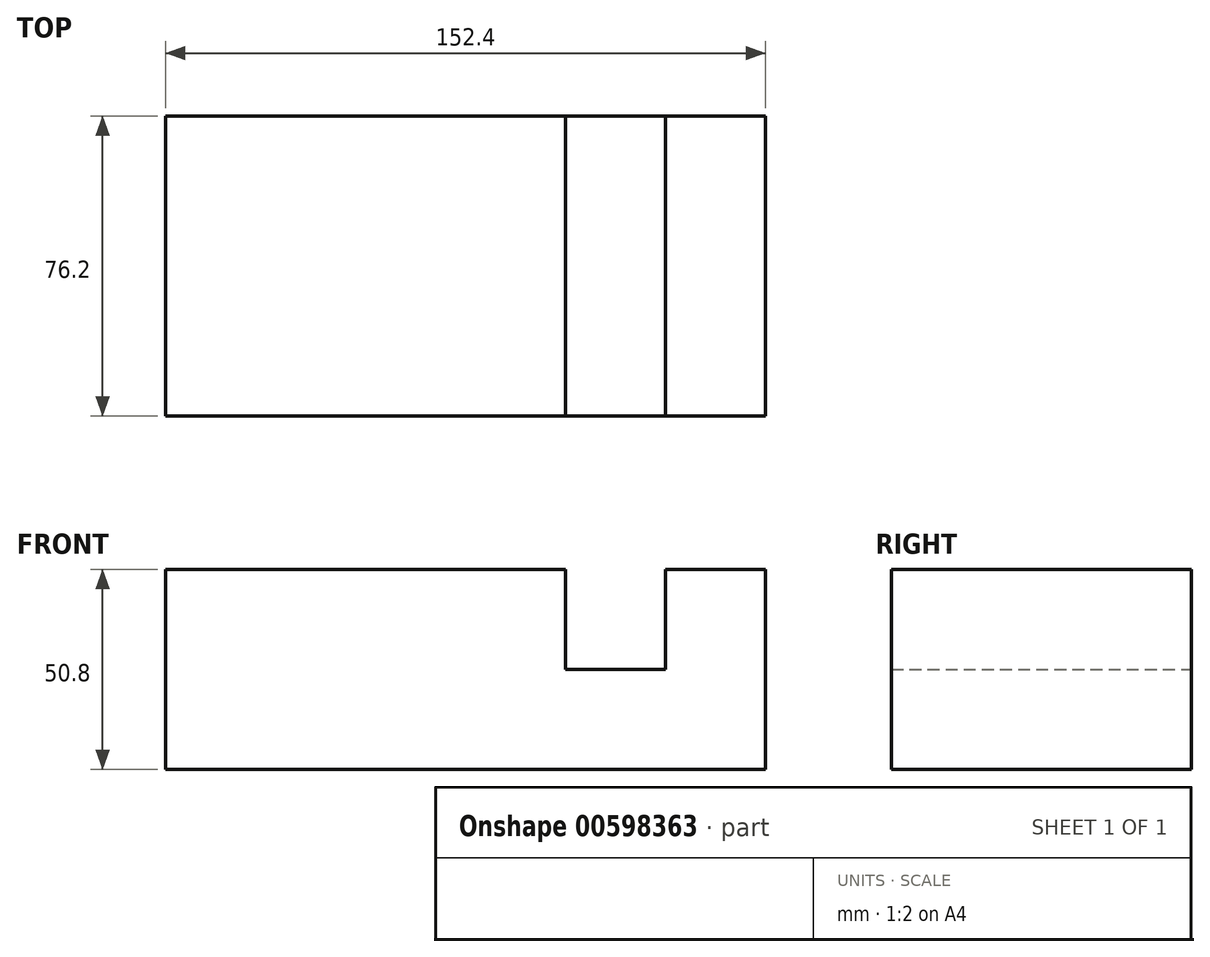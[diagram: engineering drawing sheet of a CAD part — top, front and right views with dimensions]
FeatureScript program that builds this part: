
annotation { "Feature Type Name" : "Feature", "Feature Type Description" : "" }
export const myFeature = defineFeature(function(context is Context, id is Id, definition is map)
    precondition{}
    {
        {
            var Q0;
            Q0=qCreatedBy(makeId("Front.planeOp"),FACE);
            var sketch = newSketch(context, id + "F0", { "sketchPlane" : qUnion([Q0])});
            skLineSegment(sketch, "E0", {"start": v(0, 0) * mm, "end": v(0, 50.8) * mm});
            skLineSegment(sketch, "E1", {"start": v(0, 50.8) * mm, "end": v(101.6, 50.8) * mm});
            skLineSegment(sketch, "E2", {"start": v(101.6, 50.8) * mm, "end": v(101.6, 25.4) * mm});
            skLineSegment(sketch, "E3", {"start": v(101.6, 25.4) * mm, "end": v(127, 25.4) * mm});
            skLineSegment(sketch, "E4", {"start": v(127, 25.4) * mm, "end": v(127, 50.8) * mm});
            skLineSegment(sketch, "E5", {"start": v(127, 50.8) * mm, "end": v(152.4, 50.8) * mm});
            skLineSegment(sketch, "E6", {"start": v(0, 0) * mm, "end": v(152.4, 0) * mm});
            skLineSegment(sketch, "E7", {"start": v(152.4, 50.8) * mm, "end": v(152.4, 0) * mm});
            skSolve(sketch);
        }
        {
            var Q0;
            Q0 = qSketchRegion(id + "F0", true);
            extrude(context, id + "F1", {"entities" : qUnion([Q0]), "depth" : 76.2 * mm, "offsetDistance" : 25.4 * mm});
        }
    });
